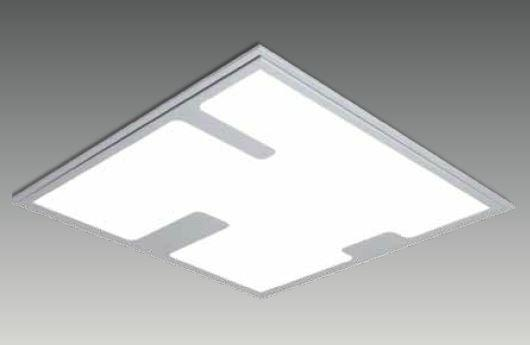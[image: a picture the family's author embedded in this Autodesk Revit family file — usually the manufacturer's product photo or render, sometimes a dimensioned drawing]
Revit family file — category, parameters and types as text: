
# Revit family: G 6060 STL
name_source: partatom
category: Lighting Fixtures
revit_build: Autodesk Revit 2017 (Build: 20160225_1515(x64)
units: mm (PartAtom-declared; Revit-internal decimal feet)

## family parameters
Always vertical = Yes
Cut with Voids When Loaded = No
Host = Ceiling
Light Source = Yes
OmniClass Number = 23.80.70.11
OmniClass Title = Luminaries for Internal Lighting
Part Type = Normal
Room Calculation Point = No
Round Connector Dimension = Use Diameter
Shared = No

## types (4) — shared parameters
Color Filter = 16777215
Dimming Lamp Color Temperature Shift = <None>
Emit Shape Visible in Rendering = Yes
Emit from Rectangle Length = 570 mm  [stored 1.87008 ft]
Emit from Rectangle Width = 570 mm  [stored 1.87008 ft]
Light Source Symbol Size = 610 mm
Manufacturer = ARLIGHT
Type Image = G 6060 STL.JPG

## per-type parameters (varying)
| type | Wattage Comments |
| GSTL.6060.36.30 | 36 |
| GSTL.6060.36.40 | 36 |
| GSTL.6060.28.30 | 28 |
| GSTL.6060.28.40 | 28 |

note: [stored X ft] marks values corroborated as IEEE doubles in the binary element streams (Revit-internal decimal feet)

## geometry (parser evidence)
native form markers: Sweep x2
no freeform markers — native parametric forms only
